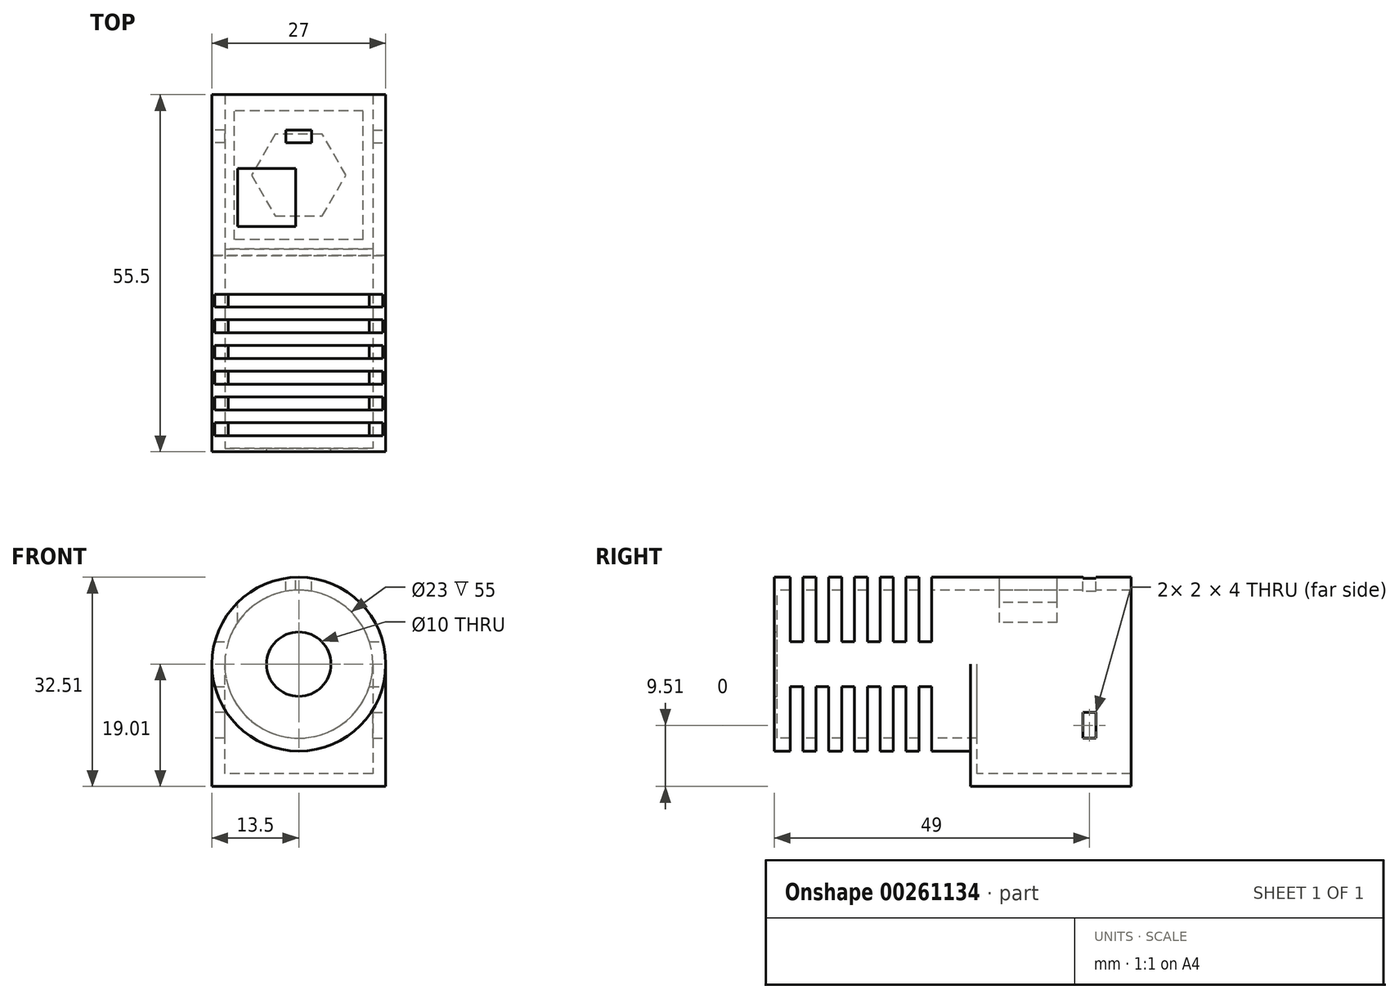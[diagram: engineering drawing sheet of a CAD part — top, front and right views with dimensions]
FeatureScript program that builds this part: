
annotation { "Feature Type Name" : "Feature", "Feature Type Description" : "" }
export const myFeature = defineFeature(function(context is Context, id is Id, definition is map)
    precondition{}
    {
        {
            var Q0;
            Q0=qCreatedBy(makeId("Front.planeOp"),FACE);
            var sketch = newSketch(context, id + "F0", { "sketchPlane" : qUnion([Q0])});
            skCircle(sketch, "E0", {"center": v(0, 0) * mm, "radius": 13.5 * mm});
            skCircle(sketch, "E1", {"center": v(0, 0) * mm, "radius": 11.5 * mm});
            skSolve(sketch);
        }
        {
            var Q0;
            Q0=qSketchRegion(id+"F0",true);
            extrude(context, id + "F1", {"entities" : qUnion([Q0]), "oppositeDirection" : true, "depth" : 30 * mm});
        }
        {
            var Q0;
            Q0=qCreatedBy(makeId("Front.planeOp"),FACE);
            var sketch = newSketch(context, id + "F2", { "sketchPlane" : qUnion([Q0])});
            skCircle(sketch, "E2", {"center": v(0, 0) * mm, "radius": 13.5 * mm});
            skCircle(sketch, "E3", {"center": v(0, 0) * mm, "radius": 5 * mm});
            skSolve(sketch);
        }
        {
            var Q0;
            Q0=qSketchRegion(id+"F2",true);
            extrude(context, id + "F3", {"entities" : qUnion([Q0]), "operationType" : NewBodyOperationType.ADD, "depth" : 0.5 * mm});
        }
        {
            var Q0;
            Q0=qCreatedBy(makeId("Top.planeOp"),FACE);
            cPlane(context, id + "F4", {"entities" : qUnion([Q0]), "cplaneType" : CPlaneType.OFFSET, "offset" : 13.5 * mm, "width" : 150 * mm, "height" : 150 * mm});
        }
        {
            var Q0;
            Q0=qCreatedBy(id+"F4.planeOp",FACE);
            var sketch = newSketch(context, id + "F5", { "sketchPlane" : qUnion([Q0])});
            skLineSegment(sketch, "E4", {"start": v(-13.5, 0) * mm, "end": v(13.5, 0) * mm});
            skLineSegment(sketch, "E5", {"start": v(-13.5, 2) * mm, "end": v(-13.5, 4) * mm});
            skLineSegment(sketch, "E6", {"start": v(-13.5, 26) * mm, "end": v(13.5, 26) * mm});
            skLineSegment(sketch, "E7", {"start": v(13.5, 24) * mm, "end": v(13.5, 22) * mm});
            skLineSegment(sketch, "E8.0.1.0", {"start": v(-13.5, 2) * mm, "end": v(13.5, 2) * mm});
            skLineSegment(sketch, "E8.0.2.0", {"start": v(-13.5, 4) * mm, "end": v(13.5, 4) * mm});
            skLineSegment(sketch, "E8.0.3.0", {"start": v(-13.5, 6) * mm, "end": v(13.5, 6) * mm});
            skLineSegment(sketch, "E8.0.4.0", {"start": v(-13.5, 8) * mm, "end": v(13.5, 8) * mm});
            skLineSegment(sketch, "E8.0.5.0", {"start": v(-13.5, 10) * mm, "end": v(13.5, 10) * mm});
            skLineSegment(sketch, "E8.0.6.0", {"start": v(-13.5, 12) * mm, "end": v(13.5, 12) * mm});
            skLineSegment(sketch, "E8.0.7.0", {"start": v(-13.5, 14) * mm, "end": v(13.5, 14) * mm});
            skLineSegment(sketch, "E8.0.8.0", {"start": v(-13.5, 16) * mm, "end": v(13.5, 16) * mm});
            skLineSegment(sketch, "E8.0.9.0", {"start": v(-13.5, 18) * mm, "end": v(13.5, 18) * mm});
            skLineSegment(sketch, "E8.0.10.0", {"start": v(-13.5, 20) * mm, "end": v(13.5, 20) * mm});
            skLineSegment(sketch, "E8.0.11.0", {"start": v(-13.5, 22) * mm, "end": v(13.5, 22) * mm});
            skLineSegment(sketch, "E8.0.12.0", {"start": v(-13.5, 24) * mm, "end": v(13.5, 24) * mm});
            skLineSegment(sketch, "E9.trimOffspring", {"start": v(-13.5, 22) * mm, "end": v(-13.5, 24) * mm});
            skLineSegment(sketch, "E10.trimOffspring", {"start": v(13.5, 20) * mm, "end": v(13.5, 18) * mm});
            skLineSegment(sketch, "E11.trimOffspring", {"start": v(-13.5, 18) * mm, "end": v(-13.5, 20) * mm});
            skLineSegment(sketch, "E12.trimOffspring", {"start": v(13.5, 16) * mm, "end": v(13.5, 14) * mm});
            skLineSegment(sketch, "E13.trimOffspring", {"start": v(-13.5, 14) * mm, "end": v(-13.5, 16) * mm});
            skLineSegment(sketch, "E14.trimOffspring", {"start": v(13.5, 12) * mm, "end": v(13.5, 10) * mm});
            skLineSegment(sketch, "E15.trimOffspring", {"start": v(-13.5, 10) * mm, "end": v(-13.5, 12) * mm});
            skLineSegment(sketch, "E16.trimOffspring", {"start": v(13.5, 8) * mm, "end": v(13.5, 6) * mm});
            skLineSegment(sketch, "E17.trimOffspring", {"start": v(-13.5, 6) * mm, "end": v(-13.5, 8) * mm});
            skLineSegment(sketch, "E18.trimOffspring", {"start": v(13.5, 4) * mm, "end": v(13.5, 2) * mm});
            skLineSegment(sketch, "E19", {"start": v(0, -4) * mm, "end": v(0, -5) * mm});
            skSolve(sketch);
        }
        {
            var Q0;
            Q0=qSketchRegion(id+"F5",true);
            extrude(context, id + "F6", {"entities" : qUnion([Q0]), "operationType" : NewBodyOperationType.REMOVE, "oppositeDirection" : true, "depth" : 10 * mm});
        }
        {
            var Q0;
            Q0=qCreatedBy(makeId("Top.planeOp"),FACE);
            cPlane(context, id + "F7", {"entities" : qUnion([Q0]), "cplaneType" : CPlaneType.OFFSET, "offset" : 13.5 * mm, "oppositeDirection" : true, "width" : 150 * mm, "height" : 150 * mm});
        }
        {
            var Q0;
            Q0=qCreatedBy(id+"F7.planeOp",FACE);
            var sketch = newSketch(context, id + "F8", { "sketchPlane" : qUnion([Q0])});
            skLineSegment(sketch, "E20", {"start": v(13.5, 2) * mm, "end": v(13.5, 4) * mm});
            skLineSegment(sketch, "E21", {"start": v(-13.5, 2) * mm, "end": v(-13.5, 4) * mm});
            skLineSegment(sketch, "E22.0.1.0", {"start": v(-13.5, 2) * mm, "end": v(13.5, 2) * mm});
            skLineSegment(sketch, "E22.0.2.0", {"start": v(-13.5, 4) * mm, "end": v(13.5, 4) * mm});
            skLineSegment(sketch, "E22.0.3.0", {"start": v(-13.5, 6) * mm, "end": v(13.5, 6) * mm});
            skLineSegment(sketch, "E22.0.4.0", {"start": v(-13.5, 8) * mm, "end": v(13.5, 8) * mm});
            skLineSegment(sketch, "E22.0.5.0", {"start": v(-13.5, 10) * mm, "end": v(13.5, 10) * mm});
            skLineSegment(sketch, "E22.0.6.0", {"start": v(-13.5, 12) * mm, "end": v(13.5, 12) * mm});
            skLineSegment(sketch, "E22.0.7.0", {"start": v(-13.5, 14) * mm, "end": v(13.5, 14) * mm});
            skLineSegment(sketch, "E22.0.8.0", {"start": v(-13.5, 16) * mm, "end": v(13.5, 16) * mm});
            skLineSegment(sketch, "E22.0.9.0", {"start": v(-13.5, 18) * mm, "end": v(13.5, 18) * mm});
            skLineSegment(sketch, "E22.0.10.0", {"start": v(-13.5, 20) * mm, "end": v(13.5, 20) * mm});
            skLineSegment(sketch, "E22.0.11.0", {"start": v(-13.5, 22) * mm, "end": v(13.5, 22) * mm});
            skLineSegment(sketch, "E22.0.12.0", {"start": v(-13.5, 24) * mm, "end": v(13.5, 24) * mm});
            skLineSegment(sketch, "E23.trimOffspring", {"start": v(-13.5, 6) * mm, "end": v(-13.5, 8) * mm});
            skLineSegment(sketch, "E24.trimOffspring", {"start": v(13.5, 6) * mm, "end": v(13.5, 8) * mm});
            skLineSegment(sketch, "E25.trimOffspring", {"start": v(-13.5, 4) * mm, "end": v(-13.5, 2) * mm});
            skLineSegment(sketch, "E26.trimOffspring", {"start": v(-13.5, 8) * mm, "end": v(-13.5, 6) * mm});
            skLineSegment(sketch, "E27.trimOffspring", {"start": v(-13.5, 10) * mm, "end": v(-13.5, 12) * mm});
            skLineSegment(sketch, "E28.trimOffspring", {"start": v(13.5, 10) * mm, "end": v(13.5, 12) * mm});
            skLineSegment(sketch, "E29.trimOffspring", {"start": v(-13.5, 12) * mm, "end": v(-13.5, 10) * mm});
            skLineSegment(sketch, "E30.trimOffspring", {"start": v(-13.5, 14) * mm, "end": v(-13.5, 16) * mm});
            skLineSegment(sketch, "E31.trimOffspring", {"start": v(13.5, 14) * mm, "end": v(13.5, 16) * mm});
            skLineSegment(sketch, "E32.trimOffspring", {"start": v(-13.5, 16) * mm, "end": v(-13.5, 14) * mm});
            skLineSegment(sketch, "E33.trimOffspring", {"start": v(13.5, 18) * mm, "end": v(13.5, 20) * mm});
            skLineSegment(sketch, "E34.trimOffspring", {"start": v(-13.5, 20) * mm, "end": v(-13.5, 18) * mm});
            skLineSegment(sketch, "E35.trimOffspring", {"start": v(-13.5, 22) * mm, "end": v(-13.5, 24) * mm});
            skLineSegment(sketch, "E36.trimOffspring", {"start": v(13.5, 22) * mm, "end": v(13.5, 24) * mm});
            skLineSegment(sketch, "E37.trimOffspring", {"start": v(-13.5, 24) * mm, "end": v(-13.5, 22) * mm});
            skSolve(sketch);
        }
        {
            var Q0;
            Q0=qSketchRegion(id+"F8",true);
            extrude(context, id + "F9", {"entities" : qUnion([Q0]), "operationType" : NewBodyOperationType.REMOVE, "depth" : 10 * mm});
        }
        {
            var Q0;
            Q0=makeQuery(id+"F1.opExtrude","CAP_FACE",FACE,{"disambiguationData":[OSD([sQuery(id+"F0.wireOp",EDGE,"E0"),sQuery(id+"F0.wireOp",EDGE,"E1")])],"isStart":false});
            var sketch = newSketch(context, id + "F10", { "sketchPlane" : qUnion([Q0])});
            skArc(sketch, "E38", {"start": v(11.5, -7.07) * mm, "mid": v(0, 13.5) * mm, "end": v(-11.5, -7.07) * mm});
            skLineSegment(sketch, "E39", {"start": v(-13.5, 0) * mm, "end": v(-13.5, -19) * mm});
            skLineSegment(sketch, "E40", {"start": v(-13.5, -19) * mm, "end": v(13.5, -19) * mm});
            skLineSegment(sketch, "E41", {"start": v(13.5, -19) * mm, "end": v(13.5, 0) * mm});
            skLineSegment(sketch, "E42", {"start": v(-11.5, 0) * mm, "end": v(-11.5, -17) * mm});
            skLineSegment(sketch, "E43", {"start": v(-11.5, -17) * mm, "end": v(11.5, -17) * mm});
            skLineSegment(sketch, "E44", {"start": v(11.5, -17) * mm, "end": v(11.5, 0) * mm});
            skCircle(sketch, "E45", {"center": v(0, 0) * mm, "radius": 11.5 * mm});
            skSolve(sketch);
        }
        {
            var Q0;
            {var subQ0=sQuery(id+"F10.wireOp",EDGE,"E38");var subQ1=makeQuery(id+"F10.imprint","INTERSECT",VERTEX,{"derivedFrom":[subQ0,sQuery(id+"F10.wireOp",EDGE,"E39")]});Q0=makeQuery(id+"F10.imprint","IMPRINT",FACE,{"disambiguationData":[TD([[makeQuery(id+"F10.imprint","IMPRINT",EDGE,{"disambiguationData":[TD([[subQ1,-1.0]])],"derivedFrom":subQ0}),-1.0]])]});}
            var Q1;
            {var subQ0=sQuery(id+"F10.wireOp",EDGE,"E39");Q1=makeQuery(id+"F10.imprint","IMPRINT",FACE,{"disambiguationData":[TD([[makeQuery(id+"F10.imprint","IMPRINT",EDGE,{"derivedFrom":subQ0}),1.0]])]});}
            extrude(context, id + "F11", {"entities" : qUnion([Q0, Q1]), "operationType" : NewBodyOperationType.ADD, "depth" : 25 * mm});
        }
        {
            var Q0;
            Q0=makeQuery(id+"F1.opExtrude","CAP_FACE",FACE,{"disambiguationData":[OSD([sQuery(id+"F0.wireOp",EDGE,"E0"),sQuery(id+"F0.wireOp",EDGE,"E1")])],"isStart":false});
            var sketch = newSketch(context, id + "F12", { "sketchPlane" : qUnion([Q0])});
            skCircle(sketch, "E46", {"center": v(0, 0) * mm, "radius": 13.5 * mm});
            skLineSegment(sketch, "E47", {"start": v(-13.5, 0) * mm, "end": v(-13.5, -19) * mm});
            skLineSegment(sketch, "E48", {"start": v(-13.5, -19) * mm, "end": v(13.5, -19) * mm});
            skLineSegment(sketch, "E49", {"start": v(13.5, -19) * mm, "end": v(13.5, 0) * mm});
            skSolve(sketch);
        }
        {
            var Q0;
            {var subQ0=sQuery(id+"F12.wireOp",EDGE,"E47");Q0=makeQuery(id+"F12.imprint","IMPRINT",FACE,{"disambiguationData":[TD([[makeQuery(id+"F12.imprint","IMPRINT",EDGE,{"derivedFrom":subQ0}),1.0]])]});}
            var Q1;
            {var subQ1=sQuery(id+"F0.wireOp",EDGE,"E1");Q1=makeQuery(id+"F12.imprint","IMPRINT",FACE,{"disambiguationData":[TD([[makeQuery(id+"F12.imprint","IMPRINT",EDGE,{"derivedFrom":makeQuery(id+"F1.opExtrude","CAP_EDGE",EDGE,{"disambiguationData":[OSD([subQ1])],"isStart":false})}),1.0]])]});}
            extrude(context, id + "F13", {"entities" : qUnion([Q0, Q1]), "operationType" : NewBodyOperationType.ADD, "depth" : 1 * mm});
        }
        {
            var Q0;
            Q0=makeQuery(id+"F11.opExtrude","SWEPT_FACE",FACE,{"disambiguationData":[OSD([sQuery(id+"F10.wireOp",EDGE,"E40")])]});
            var sketch = newSketch(context, id + "F14", { "sketchPlane" : qUnion([Q0])});
            skCircle(sketch, "E50.cCircle", {"center": v(0, -42.5) * mm, "radius": 6.35 * mm, "construction": true});
            skLineSegment(sketch, "E50.0", {"start": v(3.67, -36.15) * mm, "end": v(7.33, -42.5) * mm});
            skLineSegment(sketch, "E50.1", {"start": v(7.33, -42.5) * mm, "end": v(3.67, -48.85) * mm});
            skLineSegment(sketch, "E50.2", {"start": v(3.67, -48.85) * mm, "end": v(-3.67, -48.85) * mm});
            skLineSegment(sketch, "E50.3", {"start": v(-3.67, -48.85) * mm, "end": v(-7.33, -42.5) * mm});
            skLineSegment(sketch, "E50.4", {"start": v(-7.33, -42.5) * mm, "end": v(-3.67, -36.15) * mm});
            skLineSegment(sketch, "E50.5", {"start": v(-3.67, -36.15) * mm, "end": v(3.67, -36.15) * mm});
            skPoint(sketch, "E50.0.midPoint", {"position": v(5.5, -39.32) * mm});
            skPoint(sketch, "E51", {"position": v(-13.5, -30) * mm});
            skPoint(sketch, "E52", {"position": v(-13.5, -55) * mm});
            skLineSegment(sketch, "E53.bottom", {"start": v(10, -32.5) * mm, "end": v(-10, -32.5) * mm});
            skLineSegment(sketch, "E53.top", {"start": v(10, -52.5) * mm, "end": v(-10, -52.5) * mm});
            skLineSegment(sketch, "E53.left", {"start": v(10, -32.5) * mm, "end": v(10, -52.5) * mm});
            skLineSegment(sketch, "E53.right", {"start": v(-10, -32.5) * mm, "end": v(-10, -52.5) * mm});
            skSolve(sketch);
        }
        {
            var Q0;
            Q0=qSketchRegion(id+"F14",true);
            extrude(context, id + "F15", {"entities" : qUnion([Q0]), "operationType" : NewBodyOperationType.ADD, "depth" : 7 / 812.8 * mm});
        }
        {
            var Q0;
            Q0=qCreatedBy(id+"F4.planeOp",FACE);
            var sketch = newSketch(context, id + "F16", { "sketchPlane" : qUnion([Q0])});
            skLineSegment(sketch, "E54", {"start": v(-2, 49.5) * mm, "end": v(2, 49.5) * mm});
            skLineSegment(sketch, "E55", {"start": v(2, 49.5) * mm, "end": v(2, 47.5) * mm});
            skLineSegment(sketch, "E56", {"start": v(2, 47.5) * mm, "end": v(-2, 47.5) * mm});
            skLineSegment(sketch, "E57", {"start": v(-2, 47.5) * mm, "end": v(-2, 49.5) * mm});
            skSolve(sketch);
        }
        {
            var Q0;
            Q0=makeQuery(id+"F16.imprint","IMPRINT",FACE,{"disambiguationData":[TD([[makeQuery(id+"F16.imprint","IMPRINT",EDGE,{"derivedFrom":sQuery(id+"F16.wireOp",EDGE,"E54")}),-1.0]])]});
            extrude(context, id + "F17", {"entities" : qUnion([Q0]), "operationType" : NewBodyOperationType.REMOVE, "oppositeDirection" : true, "depth" : 3 * mm});
        }
        {
            var Q0;
            Q0=makeQuery(id+"F11.opExtrude","SWEPT_FACE",FACE,{"disambiguationData":[OSD([sQuery(id+"F10.wireOp",EDGE,"E39")])]});
            var sketch = newSketch(context, id + "F18", { "sketchPlane" : qUnion([Q0])});
            skLineSegment(sketch, "E58.bottom", {"start": v(49.5, -11.5) * mm, "end": v(47.5, -11.5) * mm});
            skLineSegment(sketch, "E58.top", {"start": v(49.5, -7.5) * mm, "end": v(47.5, -7.5) * mm});
            skLineSegment(sketch, "E58.left", {"start": v(49.5, -11.5) * mm, "end": v(49.5, -7.5) * mm});
            skLineSegment(sketch, "E58.right", {"start": v(47.5, -11.5) * mm, "end": v(47.5, -7.5) * mm});
            skPoint(sketch, "E58.middle", {"position": v(48.5, -9.5) * mm});
            skSolve(sketch);
        }
        {
            var Q0;
            Q0 = qSketchRegion(id + "F18", true);
            extrude(context, id + "F19", {"entities" : qUnion([Q0]), "operationType" : NewBodyOperationType.REMOVE, "oppositeDirection" : true, "depth" : 2 * mm});
        }
        {
            var Q0;
            Q0=makeQuery(id+"F11.opExtrude","SWEPT_FACE",FACE,{"disambiguationData":[OSD([sQuery(id+"F10.wireOp",EDGE,"E41")])]});
            var sketch = newSketch(context, id + "F20", { "sketchPlane" : qUnion([Q0])});
            skLineSegment(sketch, "E59.bottom", {"start": v(-47.5, -11.5) * mm, "end": v(-49.5, -11.5) * mm});
            skLineSegment(sketch, "E59.top", {"start": v(-47.5, -7.5) * mm, "end": v(-49.5, -7.5) * mm});
            skLineSegment(sketch, "E59.left", {"start": v(-47.5, -11.5) * mm, "end": v(-47.5, -7.5) * mm});
            skLineSegment(sketch, "E59.right", {"start": v(-49.5, -11.5) * mm, "end": v(-49.5, -7.5) * mm});
            skPoint(sketch, "E59.middle", {"position": v(-48.5, -9.5) * mm});
            skSolve(sketch);
        }
        {
            var Q0;
            Q0=makeQuery(id+"F20.imprint","IMPRINT",FACE,{"disambiguationData":[TD([[makeQuery(id+"F20.imprint","IMPRINT",EDGE,{"derivedFrom":sQuery(id+"F20.wireOp",EDGE,"E59.bottom")}),-1.0]])]});
            extrude(context, id + "F21", {"entities" : qUnion([Q0]), "operationType" : NewBodyOperationType.REMOVE, "oppositeDirection" : true, "depth" : 2 * mm});
        }
        {
            var Q0;
            Q0=qCreatedBy(id+"F4.planeOp",FACE);
            var sketch = newSketch(context, id + "F22", { "sketchPlane" : qUnion([Q0])});
            skLineSegment(sketch, "E60.bottom", {"start": v(-0.5, 43.5) * mm, "end": v(-9.5, 43.5) * mm});
            skLineSegment(sketch, "E60.top", {"start": v(-0.5, 34.5) * mm, "end": v(-9.5, 34.5) * mm});
            skLineSegment(sketch, "E60.left", {"start": v(-0.5, 43.5) * mm, "end": v(-0.5, 34.5) * mm});
            skLineSegment(sketch, "E60.right", {"start": v(-9.5, 43.5) * mm, "end": v(-9.5, 34.5) * mm});
            skPoint(sketch, "E60.middle", {"position": v(-5, 39) * mm});
            skSolve(sketch);
        }
        {
            var Q0;
            Q0=makeQuery(id+"F22.imprint","IMPRINT",FACE,{"disambiguationData":[TD([[makeQuery(id+"F22.imprint","IMPRINT",EDGE,{"derivedFrom":sQuery(id+"F22.wireOp",EDGE,"E60.bottom")}),1.0]])]});
            extrude(context, id + "F23", {"entities" : qUnion([Q0]), "operationType" : NewBodyOperationType.REMOVE, "oppositeDirection" : true, "depth" : 8 * mm});
        }
    });
